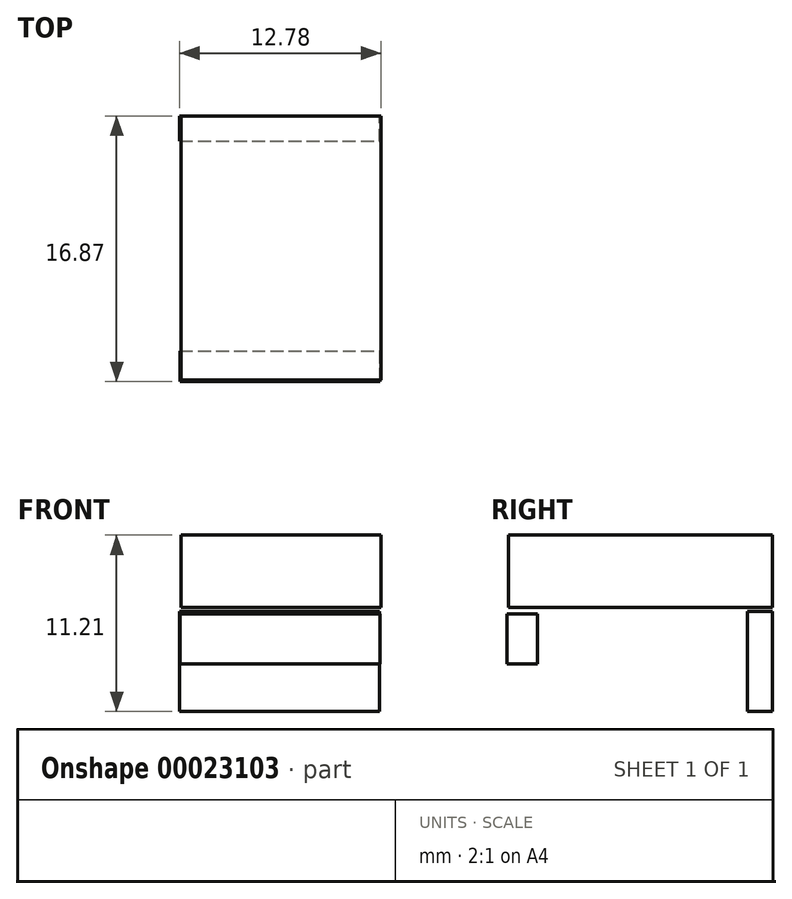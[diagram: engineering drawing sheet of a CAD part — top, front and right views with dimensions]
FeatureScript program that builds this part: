
annotation { "Feature Type Name" : "Feature", "Feature Type Description" : "" }
export const myFeature = defineFeature(function(context is Context, id is Id, definition is map)
    precondition{}
    {
        {
            var Q0;
            Q0=qCreatedBy(makeId("Front.planeOp"),FACE);
            var sketch = newSketch(context, id + "F0", { "sketchPlane" : qUnion([Q0])});
            skLineSegment(sketch, "E0.bottom", {"start": v(-15.74, 30.74) * mm, "end": v(-3.04, 30.74) * mm});
            skLineSegment(sketch, "E0.top", {"start": v(-15.74, 24.39) * mm, "end": v(-3.04, 24.39) * mm});
            skLineSegment(sketch, "E0.left", {"start": v(-15.74, 30.74) * mm, "end": v(-15.74, 24.39) * mm});
            skLineSegment(sketch, "E0.right", {"start": v(-3.04, 30.74) * mm, "end": v(-3.04, 24.39) * mm});
            skSolve(sketch);
        }
        {
            var Q0;
            Q0=makeQuery(id+"F0.imprint","IMPRINT",FACE,{"disambiguationData":[TD([[makeQuery(id+"F0.imprint","IMPRINT",EDGE,{"derivedFrom":sQuery(id+"F0.wireOp",EDGE,"E0.bottom")}),-1.0]])]});
            extrude(context, id + "F1", {"entities" : qUnion([Q0]), "depth" : 1.59 * mm});
        }
        {
            var Q0;
            Q0=qCreatedBy(makeId("Right.planeOp"),FACE);
            var sketch = newSketch(context, id + "F2", { "sketchPlane" : qUnion([Q0])});
            skLineSegment(sketch, "E1.bottom", {"start": v(-1.63, 31.18) * mm, "end": v(15.13, 31.18) * mm});
            skLineSegment(sketch, "E1.top", {"start": v(-1.63, 28.02) * mm, "end": v(15.13, 28.02) * mm});
            skLineSegment(sketch, "E1.left", {"start": v(-1.63, 31.18) * mm, "end": v(-1.63, 28.02) * mm});
            skLineSegment(sketch, "E1.right", {"start": v(15.13, 31.18) * mm, "end": v(15.13, 28.02) * mm});
            skSolve(sketch);
        }
        {
            var Q0;
            Q0=makeQuery(id+"F2.imprint","IMPRINT",FACE,{"disambiguationData":[TD([[makeQuery(id+"F2.imprint","IMPRINT",EDGE,{"derivedFrom":sQuery(id+"F2.wireOp",EDGE,"E1.bottom")}),-1.0]])]});
            extrude(context, id + "F3", {"entities" : qUnion([Q0]), "depth" : 0.25 * mm, "hasSecondDirection" : true, "secondDirectionOppositeDirection" : true, "secondDirectionDepth" : 15.97 * mm});
        }
        {
            var Q0;
            Q0=makeQuery(id+"F3.opExtrude","SWEPT_BODY",BODY,{"disambiguationData":[OSD([sQuery(id+"F2.wireOp",EDGE,"E1.bottom"),sQuery(id+"F2.wireOp",EDGE,"E1.top"),sQuery(id+"F2.wireOp",EDGE,"E1.left"),sQuery(id+"F2.wireOp",EDGE,"E1.right")])]});
            deleteBodies(context, id + "F4", {"entities" : qUnion([Q0])});
        }
        {
            var Q0;
            Q0=qCreatedBy(makeId("Front.planeOp"),FACE);
            var sketch = newSketch(context, id + "F5", { "sketchPlane" : qUnion([Q0])});
            skLineSegment(sketch, "E2.bottom", {"start": v(-15.66, 31) * mm, "end": v(-2.96, 31) * mm});
            skLineSegment(sketch, "E2.top", {"start": v(-15.66, 35.6) * mm, "end": v(-2.96, 35.6) * mm});
            skLineSegment(sketch, "E2.left", {"start": v(-15.66, 31) * mm, "end": v(-15.66, 35.6) * mm});
            skLineSegment(sketch, "E2.right", {"start": v(-2.96, 31) * mm, "end": v(-2.96, 35.6) * mm});
            skSolve(sketch);
        }
        {
            var Q0;
            Q0=makeQuery(id+"F5.imprint","IMPRINT",FACE,{"disambiguationData":[TD([[makeQuery(id+"F5.imprint","IMPRINT",EDGE,{"derivedFrom":sQuery(id+"F5.wireOp",EDGE,"E2.bottom")}),1.0]])]});
            extrude(context, id + "F6", {"entities" : qUnion([Q0]), "depth" : 16.76 * mm});
        }
        {
            var Q0;
            Q0=qCreatedBy(makeId("Front.planeOp"),FACE);
            var sketch = newSketch(context, id + "F7", { "sketchPlane" : qUnion([Q0])});
            skLineSegment(sketch, "E3.bottom", {"start": v(-15.72, 30.6) * mm, "end": v(-3.02, 30.6) * mm});
            skLineSegment(sketch, "E3.top", {"start": v(-15.72, 27.42) * mm, "end": v(-3.02, 27.42) * mm});
            skLineSegment(sketch, "E3.left", {"start": v(-15.72, 30.6) * mm, "end": v(-15.72, 27.42) * mm});
            skLineSegment(sketch, "E3.right", {"start": v(-3.02, 30.6) * mm, "end": v(-3.02, 27.42) * mm});
            skSolve(sketch);
        }
        {
            var Q0;
            Q0=makeQuery(id+"F7.imprint","IMPRINT",FACE,{"disambiguationData":[TD([[makeQuery(id+"F7.imprint","IMPRINT",EDGE,{"derivedFrom":sQuery(id+"F7.wireOp",EDGE,"E3.bottom")}),-1.0]])]});
            extrude(context, id + "F8", {"entities" : qUnion([Q0]), "operationType" : NewBodyOperationType.ADD, "depth" : 16.87 * mm, "hasSecondDirection" : true, "secondDirectionOppositeDirection" : false, "secondDirectionDepth" : 14.93 * mm});
        }
    });
